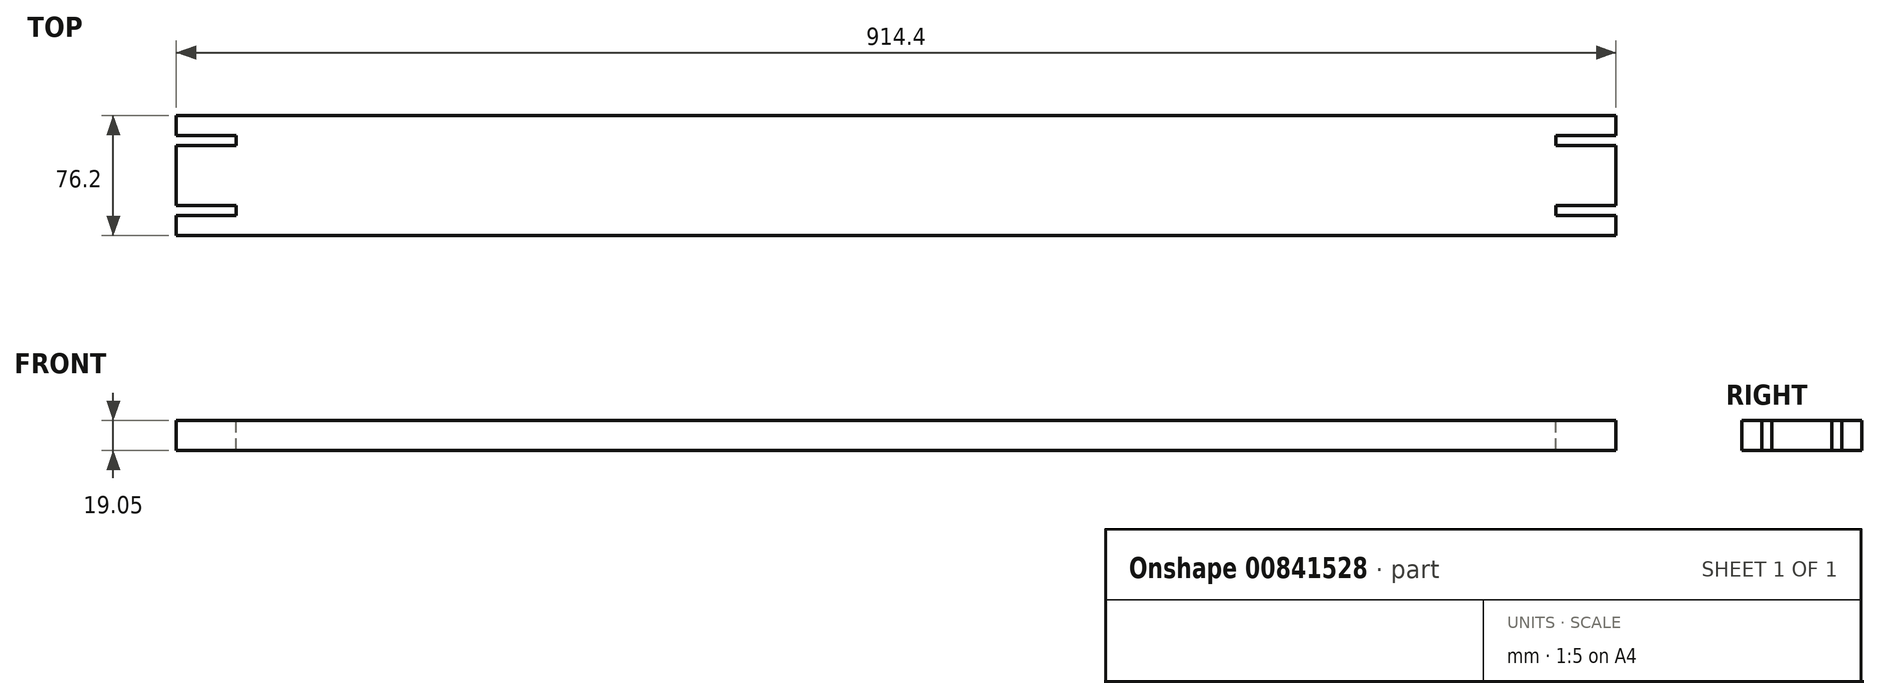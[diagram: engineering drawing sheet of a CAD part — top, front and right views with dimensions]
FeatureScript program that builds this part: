
annotation { "Feature Type Name" : "Feature", "Feature Type Description" : "" }
export const myFeature = defineFeature(function(context is Context, id is Id, definition is map)
    precondition{}
    {
        {
            var Q0;
            Q0=qCreatedBy(makeId("Top.planeOp"),FACE);
            var sketch = newSketch(context, id + "F0", { "sketchPlane" : qUnion([Q0])});
            skLineSegment(sketch, "E0.bottom", {"start": v(-457.2, 0) * mm, "end": v(457.2, 0) * mm});
            skLineSegment(sketch, "E0.top", {"start": v(-457.2, 76.2) * mm, "end": v(457.2, 76.2) * mm});
            skLineSegment(sketch, "E0.left", {"start": v(-457.2, 0) * mm, "end": v(-457.2, 76.2) * mm});
            skLineSegment(sketch, "E0.right", {"start": v(457.2, 0) * mm, "end": v(457.2, 76.2) * mm});
            skSolve(sketch);
        }
        {
            var Q0;
            Q0 = qSketchRegion(id + "F0", true);
            extrude(context, id + "F1", {"entities" : qUnion([Q0]), "depth" : 19.05 * mm, "offsetDistance" : 25.4 * mm});
        }
        {
            var Q0;
            Q0=makeQuery(id+"F1.opExtrude","CAP_FACE",FACE,{"disambiguationData":[OSD([sQuery(id+"F0.wireOp",EDGE,"E0.bottom"),sQuery(id+"F0.wireOp",EDGE,"E0.top"),sQuery(id+"F0.wireOp",EDGE,"E0.left"),sQuery(id+"F0.wireOp",EDGE,"E0.right")])],"isStart":false});
            var sketch = newSketch(context, id + "F2", { "sketchPlane" : qUnion([Q0])});
            skLineSegment(sketch, "E1.bottom", {"start": v(-457.2, 12.7) * mm, "end": v(-419.1, 12.7) * mm});
            skLineSegment(sketch, "E1.top", {"start": v(-457.2, 19.05) * mm, "end": v(-419.1, 19.05) * mm});
            skLineSegment(sketch, "E1.left", {"start": v(-457.2, 12.7) * mm, "end": v(-457.2, 19.05) * mm});
            skLineSegment(sketch, "E1.right", {"start": v(-419.1, 12.7) * mm, "end": v(-419.1, 19.05) * mm});
            skLineSegment(sketch, "E2.bottom", {"start": v(-457.2, 63.5) * mm, "end": v(-419.1, 63.5) * mm});
            skLineSegment(sketch, "E2.top", {"start": v(-457.2, 57.15) * mm, "end": v(-419.1, 57.15) * mm});
            skLineSegment(sketch, "E2.left", {"start": v(-457.2, 63.5) * mm, "end": v(-457.2, 57.15) * mm});
            skLineSegment(sketch, "E2.right", {"start": v(-419.1, 63.5) * mm, "end": v(-419.1, 57.15) * mm});
            skLineSegment(sketch, "E3.bottom", {"start": v(457.2, 63.5) * mm, "end": v(419.1, 63.5) * mm});
            skLineSegment(sketch, "E3.top", {"start": v(457.2, 57.15) * mm, "end": v(419.1, 57.15) * mm});
            skLineSegment(sketch, "E3.left", {"start": v(457.2, 63.5) * mm, "end": v(457.2, 57.15) * mm});
            skLineSegment(sketch, "E3.right", {"start": v(419.1, 63.5) * mm, "end": v(419.1, 57.15) * mm});
            skLineSegment(sketch, "E4.bottom", {"start": v(457.2, 12.7) * mm, "end": v(419.1, 12.7) * mm});
            skLineSegment(sketch, "E4.top", {"start": v(457.2, 19.05) * mm, "end": v(419.1, 19.05) * mm});
            skLineSegment(sketch, "E4.left", {"start": v(457.2, 12.7) * mm, "end": v(457.2, 19.05) * mm});
            skLineSegment(sketch, "E4.right", {"start": v(419.1, 12.7) * mm, "end": v(419.1, 19.05) * mm});
            skSolve(sketch);
        }
        {
            var Q0;
            Q0 = qSketchRegion(id + "F2", true);
            extrude(context, id + "F3", {"entities" : qUnion([Q0]), "operationType" : NewBodyOperationType.REMOVE, "endBound" : BoundingType.UP_TO_NEXT, "oppositeDirection" : true, "depth" : 25.4 * mm, "offsetDistance" : 25.4 * mm});
        }
    });
